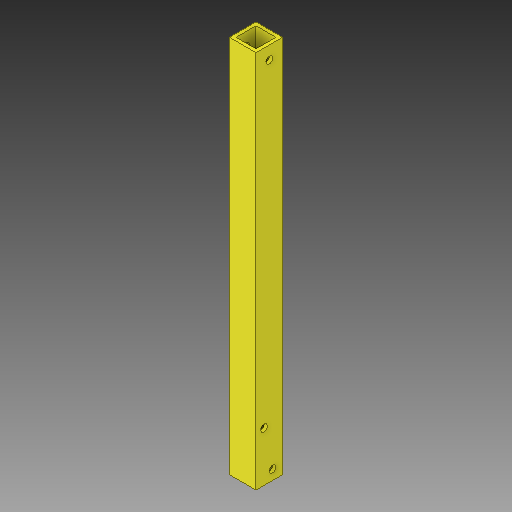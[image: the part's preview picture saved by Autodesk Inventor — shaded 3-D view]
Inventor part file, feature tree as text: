
AUTODESK INVENTOR PART (.ipt)
format: ipt  version: 2017 SP1 (Build 210196100, 196)  size: 128,512 bytes
history: native  units: in
note: dims shown in document units (in); Inventor stores cm internally (conversion verified against a paired STEP export)
features: extrude x2, sketch x2
ambient origin geometry x8: Origin, YZ Plane, XZ Plane, XY Plane, X Axis, Y Axis, Z Axis, Center Point
bodies: Solid1 (feature_tree)
feature tree (4):
  extrude  "Extrusion1"  Depth=0.125in
  extrude  "Extrusion2"  Depth=14.25in
  sketch  "Sketch1"  dims[d0=1.0in d1=0.125in]
  sketch  "Sketch2"  dims[d2=14.25in d3=0.0in d5=0.26in d6=2.375in d9=0.26in d10=11.893in d11=10.0in d12=0.0in d15=0.298in d16=0.5in d17=0.26in d18=0.4375in d19=0.0069in d20=0.375in d22=1.5in d23=0.03in]
